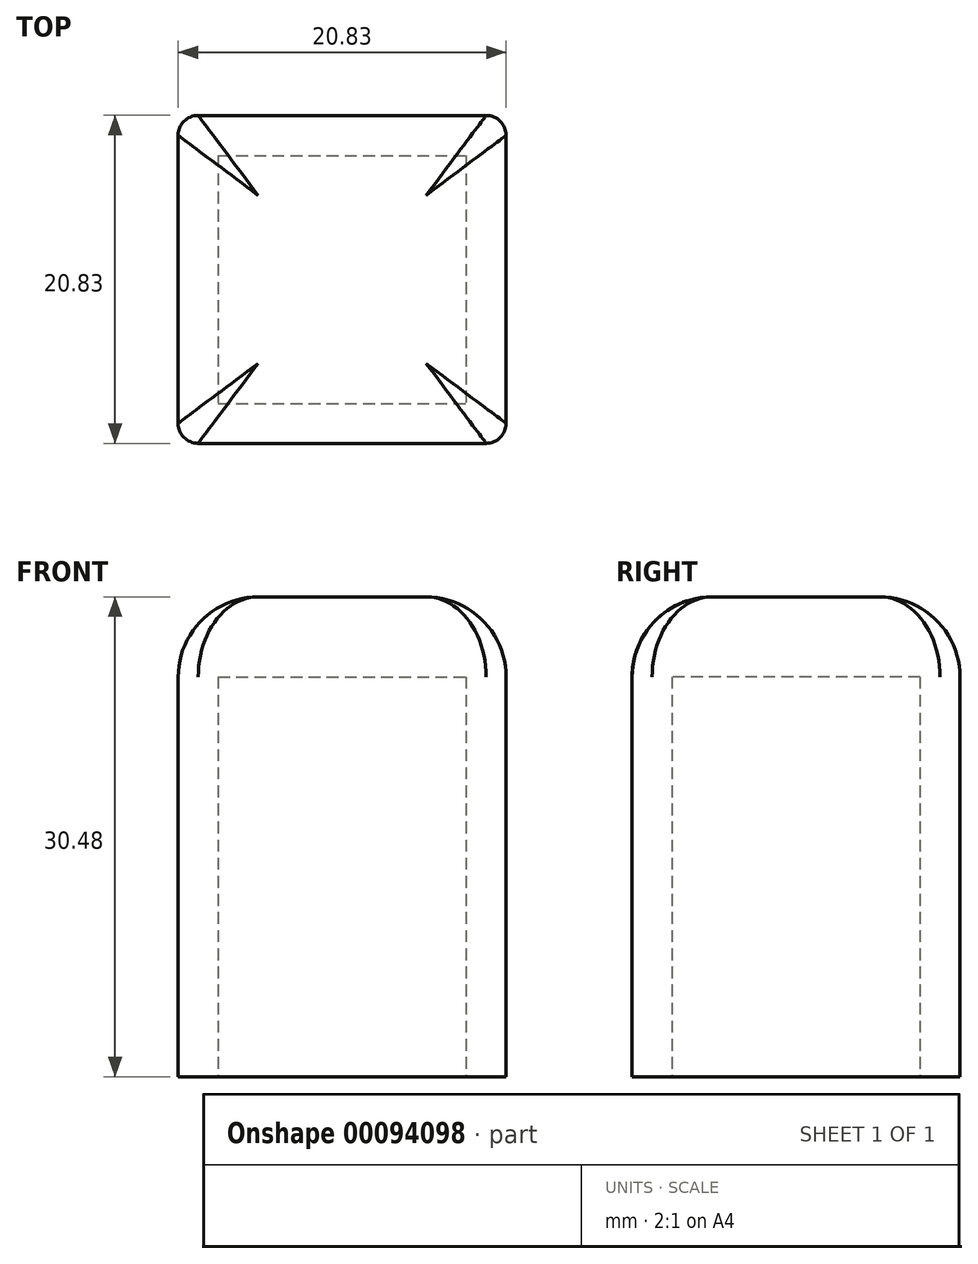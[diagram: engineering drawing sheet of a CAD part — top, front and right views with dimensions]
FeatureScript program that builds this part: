
annotation { "Feature Type Name" : "Feature", "Feature Type Description" : "" }
export const myFeature = defineFeature(function(context is Context, id is Id, definition is map)
    precondition{}
    {
        {
            var Q0;
            Q0=qCreatedBy(makeId("Top.planeOp"),FACE);
            var sketch = newSketch(context, id + "F0", { "sketchPlane" : qUnion([Q0])});
            skLineSegment(sketch, "E0.bottom", {"start": v(0, 0) * mm, "end": v(20.83, 0) * mm});
            skLineSegment(sketch, "E0.top", {"start": v(0, 20.83) * mm, "end": v(20.83, 20.83) * mm});
            skLineSegment(sketch, "E0.left", {"start": v(0, 0) * mm, "end": v(0, 20.83) * mm});
            skLineSegment(sketch, "E0.right", {"start": v(20.83, 0) * mm, "end": v(20.83, 20.83) * mm});
            skLineSegment(sketch, "E1.bottom", {"start": v(2.54, 18.29) * mm, "end": v(18.29, 18.29) * mm});
            skLineSegment(sketch, "E1.top", {"start": v(2.54, 2.54) * mm, "end": v(18.29, 2.54) * mm});
            skLineSegment(sketch, "E1.left", {"start": v(2.54, 18.29) * mm, "end": v(2.54, 2.54) * mm});
            skLineSegment(sketch, "E1.right", {"start": v(18.29, 18.29) * mm, "end": v(18.29, 2.54) * mm});
            skLineSegment(sketch, "E2", {"start": v(10.41, 20.83) * mm, "end": v(10.41, 0) * mm, "construction": true});
            skLineSegment(sketch, "E3", {"start": v(10.41, 0) * mm, "end": v(0, 10.41) * mm, "construction": true});
            skLineSegment(sketch, "E4", {"start": v(0, 10.41) * mm, "end": v(20.83, 10.41) * mm, "construction": true});
            skPoint(sketch, "E5", {"position": v(10.41, 18.29) * mm});
            skPoint(sketch, "E6", {"position": v(18.29, 10.41) * mm});
            skSolve(sketch);
        }
        {
            var Q0;
            Q0=makeQuery(id+"F0.imprint","IMPRINT",FACE,{"disambiguationData":[TD([[makeQuery(id+"F0.imprint","IMPRINT",EDGE,{"derivedFrom":sQuery(id+"F0.wireOp",EDGE,"E0.bottom")}),1.0]])]});
            extrude(context, id + "F1", {"entities" : qUnion([Q0]), "depth" : 25.4 * mm, "offsetDistance" : 25.4 * mm});
        }
        {
            var Q0;
            Q0=makeQuery(id+"F1.opExtrude","CAP_FACE",FACE,{"disambiguationData":[OSD([sQuery(id+"F0.wireOp",EDGE,"E0.bottom"),sQuery(id+"F0.wireOp",EDGE,"E0.top"),sQuery(id+"F0.wireOp",EDGE,"E0.left"),sQuery(id+"F0.wireOp",EDGE,"E0.right"),sQuery(id+"F0.wireOp",EDGE,"E1.bottom"),sQuery(id+"F0.wireOp",EDGE,"E1.top"),sQuery(id+"F0.wireOp",EDGE,"E1.left"),sQuery(id+"F0.wireOp",EDGE,"E1.right")])],"isStart":false});
            var sketch = newSketch(context, id + "F2", { "sketchPlane" : qUnion([Q0])});
            skLineSegment(sketch, "E7.0.0", {"start": v(20.83, 20.83) * mm, "end": v(0, 20.83) * mm});
            skLineSegment(sketch, "E7.0.1", {"start": v(0, 20.83) * mm, "end": v(0, 0) * mm});
            skLineSegment(sketch, "E7.0.2", {"start": v(0, 0) * mm, "end": v(20.83, 0) * mm});
            skLineSegment(sketch, "E7.0.3", {"start": v(20.83, 0) * mm, "end": v(20.83, 20.83) * mm});
            skSolve(sketch);
        }
        {
            var Q0;
            Q0=makeQuery(id+"F2.imprint","IMPRINT",FACE,{"disambiguationData":[TD([[makeQuery(id+"F2.imprint","IMPRINT",EDGE,{"derivedFrom":sQuery(id+"F2.wireOp",EDGE,"E7.0.0")}),-1.0]])]});
            var Q1;
            Q1=makeQuery(id+"F2.imprint","IMPRINT",FACE,{"disambiguationData":[TD([[makeQuery(id+"F2.imprint","IMPRINT",EDGE,{"derivedFrom":makeQuery(id+"F1.opExtrude","CAP_EDGE",EDGE,{"disambiguationData":[OSD([sQuery(id+"F0.wireOp",EDGE,"E1.bottom")])],"isStart":false})}),-1.0]])]});
            extrude(context, id + "F3", {"entities" : qUnion([Q0, Q1]), "operationType" : NewBodyOperationType.ADD, "depth" : 5.08 * mm, "offsetDistance" : 25.4 * mm});
        }
        {
            var Q0;
            Q0=makeQuery(id+"F3.opExtrude","CAP_EDGE",EDGE,{"disambiguationData":[OSD([sQuery(id+"F2.wireOp",EDGE,"E7.0.0")])],"isStart":false});
            var Q1;
            Q1=makeQuery(id+"F3.opExtrude","CAP_EDGE",EDGE,{"disambiguationData":[OSD([sQuery(id+"F2.wireOp",EDGE,"E7.0.3")])],"isStart":false});
            var Q2;
            Q2=makeQuery(id+"F3.opExtrude","CAP_EDGE",EDGE,{"disambiguationData":[OSD([sQuery(id+"F2.wireOp",EDGE,"E7.0.2")])],"isStart":false});
            var Q3;
            Q3=makeQuery(id+"F3.opExtrude","CAP_EDGE",EDGE,{"disambiguationData":[OSD([sQuery(id+"F2.wireOp",EDGE,"E7.0.1")])],"isStart":false});
            fillet(context, id + "F4", {"entities" : qUnion([Q0, Q1, Q2, Q3]), "radius" : 5.08 * mm, "tangentPropagation" : true, "allowEdgeOverflow" : false});
        }
        {
            var Q0;
            Q0=makeQuery(id+"F3.boolean.opBoolean","MERGE",EDGE,{"derivedFrom":[makeQuery(id+"F1.opExtrude","SWEPT_EDGE",EDGE,{"disambiguationData":[OSD([sQuery(id+"F0.wireOp",EDGE,"E0.top"),sQuery(id+"F0.wireOp",EDGE,"E0.left")])]}),makeQuery(id+"F3.opExtrude","SWEPT_EDGE",EDGE,{"disambiguationData":[OSD([sQuery(id+"F2.wireOp",EDGE,"E7.0.0"),sQuery(id+"F2.wireOp",EDGE,"E7.0.1")])]})]});
            var Q1;
            Q1=makeQuery(id+"F3.boolean.opBoolean","MERGE",EDGE,{"derivedFrom":[makeQuery(id+"F1.opExtrude","SWEPT_EDGE",EDGE,{"disambiguationData":[OSD([sQuery(id+"F0.wireOp",EDGE,"E0.top"),sQuery(id+"F0.wireOp",EDGE,"E0.right")])]}),makeQuery(id+"F3.opExtrude","SWEPT_EDGE",EDGE,{"disambiguationData":[OSD([sQuery(id+"F2.wireOp",EDGE,"E7.0.0"),sQuery(id+"F2.wireOp",EDGE,"E7.0.3")])]})]});
            var Q2;
            Q2=makeQuery(id+"F3.boolean.opBoolean","MERGE",EDGE,{"derivedFrom":[makeQuery(id+"F1.opExtrude","SWEPT_EDGE",EDGE,{"disambiguationData":[OSD([sQuery(id+"F0.wireOp",EDGE,"E0.bottom"),sQuery(id+"F0.wireOp",EDGE,"E0.right")])]}),makeQuery(id+"F3.opExtrude","SWEPT_EDGE",EDGE,{"disambiguationData":[OSD([sQuery(id+"F2.wireOp",EDGE,"E7.0.2"),sQuery(id+"F2.wireOp",EDGE,"E7.0.3")])]})]});
            var Q3;
            Q3=makeQuery(id+"F3.boolean.opBoolean","MERGE",EDGE,{"derivedFrom":[makeQuery(id+"F1.opExtrude","SWEPT_EDGE",EDGE,{"disambiguationData":[OSD([sQuery(id+"F0.wireOp",EDGE,"E0.bottom"),sQuery(id+"F0.wireOp",EDGE,"E0.left")])]}),makeQuery(id+"F3.opExtrude","SWEPT_EDGE",EDGE,{"disambiguationData":[OSD([sQuery(id+"F2.wireOp",EDGE,"E7.0.1"),sQuery(id+"F2.wireOp",EDGE,"E7.0.2")])]})]});
            fillet(context, id + "F5", {"entities" : qUnion([Q0, Q1, Q2, Q3]), "radius" : 1.27 * mm, "tangentPropagation" : true, "allowEdgeOverflow" : false});
        }
    });
